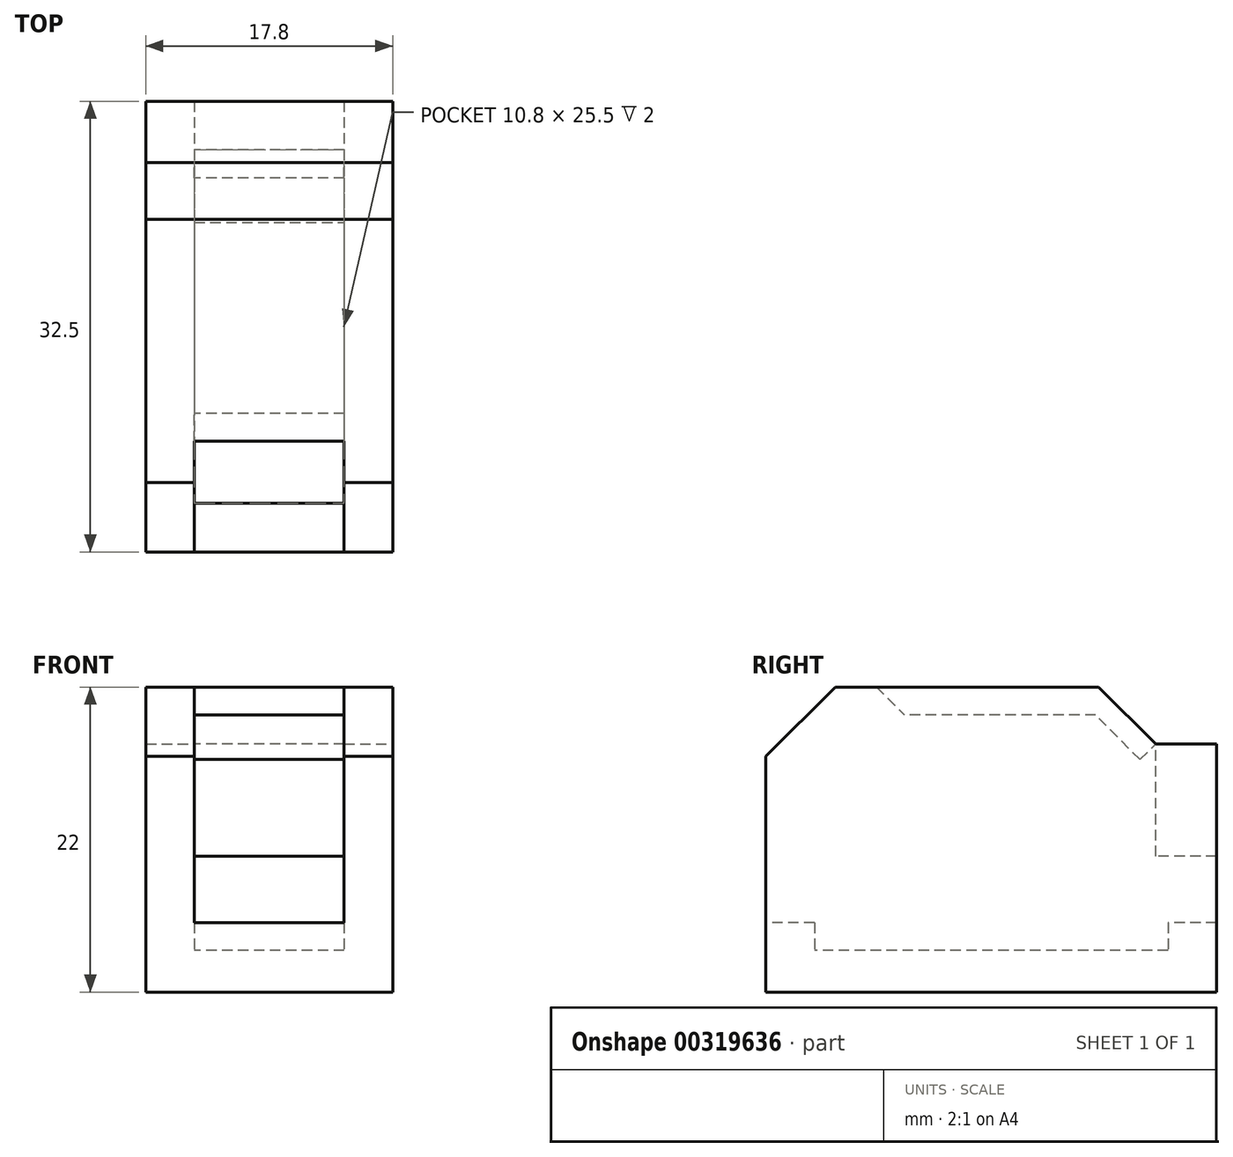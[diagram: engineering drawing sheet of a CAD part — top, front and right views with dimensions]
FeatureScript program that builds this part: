
annotation { "Feature Type Name" : "Feature", "Feature Type Description" : "" }
export const myFeature = defineFeature(function(context is Context, id is Id, definition is map)
    precondition{}
    {
        {
            var Q0;
            Q0=qCreatedBy(makeId("Top.planeOp"),FACE);
            var sketch = newSketch(context, id + "F0", { "sketchPlane" : qUnion([Q0])});
            skLineSegment(sketch, "E0.bottom", {"start": v(5.4, 12.75) * mm, "end": v(-5.4, 12.75) * mm});
            skLineSegment(sketch, "E0.top", {"start": v(5.4, -12.75) * mm, "end": v(-5.4, -12.75) * mm});
            skLineSegment(sketch, "E0.left", {"start": v(5.4, 12.75) * mm, "end": v(5.4, -12.75) * mm});
            skLineSegment(sketch, "E0.right", {"start": v(-5.4, 12.75) * mm, "end": v(-5.4, -12.75) * mm});
            skPoint(sketch, "E0.middle", {"position": v(0, 0) * mm});
            skLineSegment(sketch, "E1.0", {"start": v(-8.9, 16.25) * mm, "end": v(-8.9, -16.25) * mm});
            skLineSegment(sketch, "E1.1", {"start": v(8.9, 16.25) * mm, "end": v(-8.9, 16.25) * mm});
            skLineSegment(sketch, "E1.2", {"start": v(8.9, 16.25) * mm, "end": v(8.9, -16.25) * mm});
            skLineSegment(sketch, "E1.3", {"start": v(8.9, -16.25) * mm, "end": v(-8.9, -16.25) * mm});
            skLineSegment(sketch, "E2", {"start": v(-8.9, 0) * mm, "end": v(-5.4, 0) * mm});
            skLineSegment(sketch, "E3", {"start": v(5.4, 0) * mm, "end": v(8.9, 0) * mm});
            skLineSegment(sketch, "E4", {"start": v(-5.4, -12.75) * mm, "end": v(-5.4, -16.25) * mm});
            skLineSegment(sketch, "E5", {"start": v(5.4, -12.75) * mm, "end": v(5.4, -16.25) * mm});
            skLineSegment(sketch, "E6", {"start": v(-5.4, 12.75) * mm, "end": v(-5.4, 16.25) * mm});
            skLineSegment(sketch, "E7", {"start": v(5.4, 12.75) * mm, "end": v(5.4, 16.25) * mm});
            skLineSegment(sketch, "E8", {"start": v(5.4, 12.75) * mm, "end": v(8.9, 12.75) * mm});
            skLineSegment(sketch, "E9", {"start": v(-5.4, 12.75) * mm, "end": v(-8.9, 12.75) * mm});
            skSolve(sketch);
        }
        {
            var Q0;
            {var subQ3=sQuery(id+"F0.wireOp",EDGE,"E0.bottom");Q0=makeQuery(id+"F0.imprint","IMPRINT",FACE,{"disambiguationData":[TD([[makeQuery(id+"F0.imprint","IMPRINT",EDGE,{"derivedFrom":subQ3}),1.0]])]});}
            extrude(context, id + "F1", {"entities" : qUnion([Q0]), "depth" : 3 * mm});
        }
        {
            var Q0;
            {var subQ4=sQuery(id+"F0.wireOp",EDGE,"E2");Q0=makeQuery(id+"F0.imprint","IMPRINT",FACE,{"disambiguationData":[TD([[makeQuery(id+"F0.imprint","IMPRINT",EDGE,{"derivedFrom":subQ4}),1.0]])]});}
            var Q1;
            {var subQ3=sQuery(id+"F0.wireOp",EDGE,"E3");Q1=makeQuery(id+"F0.imprint","IMPRINT",FACE,{"disambiguationData":[TD([[makeQuery(id+"F0.imprint","IMPRINT",EDGE,{"derivedFrom":subQ3}),1.0]])]});}
            var Q2;
            {var subQ0=sQuery(id+"F0.wireOp",EDGE,"E2");Q2=makeQuery(id+"F0.imprint","IMPRINT",FACE,{"disambiguationData":[TD([[makeQuery(id+"F0.imprint","IMPRINT",EDGE,{"derivedFrom":subQ0}),-1.0]])]});}
            var Q3;
            {var subQ0=sQuery(id+"F0.wireOp",EDGE,"E3");Q3=makeQuery(id+"F0.imprint","IMPRINT",FACE,{"disambiguationData":[TD([[makeQuery(id+"F0.imprint","IMPRINT",EDGE,{"derivedFrom":subQ0}),-1.0]])]});}
            extrude(context, id + "F2", {"entities" : qUnion([Q0, Q1, Q2, Q3]), "operationType" : NewBodyOperationType.ADD, "depth" : 22 * mm});
        }
        {
            var Q0;
            Q0=makeQuery(id+"F0.imprint","IMPRINT",FACE,{"disambiguationData":[TD([[makeQuery(id+"F0.imprint","IMPRINT",EDGE,{"derivedFrom":sQuery(id+"F0.wireOp",EDGE,"E0.bottom")}),-1.0]])]});
            var Q1;
            {var subQ4=sQuery(id+"F0.wireOp",EDGE,"E6");Q1=makeQuery(id+"F0.imprint","IMPRINT",FACE,{"disambiguationData":[TD([[makeQuery(id+"F0.imprint","IMPRINT",EDGE,{"derivedFrom":subQ4}),1.0]])]});}
            var Q2;
            {var subQ3=sQuery(id+"F0.wireOp",EDGE,"E7");Q2=makeQuery(id+"F0.imprint","IMPRINT",FACE,{"disambiguationData":[TD([[makeQuery(id+"F0.imprint","IMPRINT",EDGE,{"derivedFrom":subQ3}),-1.0]])]});}
            extrude(context, id + "F3", {"entities" : qUnion([Q0, Q1, Q2]), "operationType" : NewBodyOperationType.ADD, "depth" : 5 * mm});
        }
        {
            var Q0;
            {var subQ0=sQuery(id+"F0.wireOp",EDGE,"E1.3");Q0=makeQuery(id+"F2.opExtrude","CAP_EDGE",EDGE,{"disambiguationData":[OSD([subQ0]),TDD([makeQuery(id+"F0.imprint","IMPRINT",EDGE,{"disambiguationData":[TD([[makeQuery(id+"F0.imprint","INTERSECT",VERTEX,{"derivedFrom":[sQuery(id+"F0.wireOp",EDGE,"E1.0"),subQ0]}),1.0]])],"derivedFrom":subQ0})])],"isStart":false});}
            var Q1;
            {var subQ0=sQuery(id+"F0.wireOp",EDGE,"E1.3");Q1=makeQuery(id+"F2.opExtrude","CAP_EDGE",EDGE,{"disambiguationData":[OSD([subQ0]),TDD([makeQuery(id+"F0.imprint","IMPRINT",EDGE,{"disambiguationData":[TD([[makeQuery(id+"F0.imprint","INTERSECT",VERTEX,{"derivedFrom":[sQuery(id+"F0.wireOp",EDGE,"E1.2"),subQ0]}),-1.0]])],"derivedFrom":subQ0})])],"isStart":false});}
            chamfer(context, id + "F4", {"entities" : qUnion([Q0, Q1]), "width" : 5 * mm, "tangentPropagation" : true});
        }
        {
            var Q0;
            {var subQ4=sQuery(id+"F0.wireOp",EDGE,"E6");Q0=makeQuery(id+"F0.imprint","IMPRINT",FACE,{"disambiguationData":[TD([[makeQuery(id+"F0.imprint","IMPRINT",EDGE,{"derivedFrom":subQ4}),1.0]])]});}
            var Q1;
            {var subQ3=sQuery(id+"F0.wireOp",EDGE,"E7");Q1=makeQuery(id+"F0.imprint","IMPRINT",FACE,{"disambiguationData":[TD([[makeQuery(id+"F0.imprint","IMPRINT",EDGE,{"derivedFrom":subQ3}),-1.0]])]});}
            extrude(context, id + "F5", {"entities" : qUnion([Q0, Q1]), "operationType" : NewBodyOperationType.ADD, "depth" : 17.9 * mm});
        }
        {
            var Q0;
            Q0=makeQuery(id+"F2.opExtrude","CAP_EDGE",EDGE,{"disambiguationData":[OSD([sQuery(id+"F0.wireOp",EDGE,"E8")])],"isStart":false});
            var Q1;
            Q1=makeQuery(id+"F2.opExtrude","CAP_EDGE",EDGE,{"disambiguationData":[OSD([sQuery(id+"F0.wireOp",EDGE,"E9")])],"isStart":false});
            chamfer(context, id + "F6", {"entities" : qUnion([Q0, Q1]), "width" : 5 * mm, "tangentPropagation" : true});
        }
        {
            var Q0;
            Q0=makeQuery(id+"F5.opExtrude","CAP_FACE",FACE,{"disambiguationData":[OSD([sQuery(id+"F0.wireOp",EDGE,"E1.1"),sQuery(id+"F0.wireOp",EDGE,"E1.2"),sQuery(id+"F0.wireOp",EDGE,"E7"),sQuery(id+"F0.wireOp",EDGE,"E8")])],"isStart":false});
            var sketch = newSketch(context, id + "F7", { "sketchPlane" : qUnion([Q0])});
            skLineSegment(sketch, "E10.bottom", {"start": v(8.9, 11.85) * mm, "end": v(-8.9, 11.85) * mm});
            skLineSegment(sketch, "E10.top", {"start": v(8.9, 16.25) * mm, "end": v(-8.9, 16.25) * mm});
            skLineSegment(sketch, "E10.left", {"start": v(8.9, 11.85) * mm, "end": v(8.9, 16.25) * mm});
            skLineSegment(sketch, "E10.right", {"start": v(-8.9, 11.85) * mm, "end": v(-8.9, 16.25) * mm});
            skSolve(sketch);
        }
        {
            var Q0;
            Q0=makeQuery(id+"F7.imprint","IMPRINT",FACE,{"disambiguationData":[TD([[makeQuery(id+"F7.imprint","IMPRINT",EDGE,{"derivedFrom":sQuery(id+"F7.wireOp",EDGE,"E10.top")}),1.0]])]});
            var Q1;
            {var subQ3=sQuery(id+"F7.wireOp",EDGE,"E10.left");Q1=makeQuery(id+"F7.imprint","IMPRINT",FACE,{"disambiguationData":[TD([[makeQuery(id+"F7.imprint","IMPRINT",EDGE,{"derivedFrom":subQ3}),-1.0]])]});}
            extrude(context, id + "F8", {"entities" : qUnion([Q0, Q1]), "operationType" : NewBodyOperationType.ADD, "oppositeDirection" : true, "depth" : 8.1 * mm});
        }
        {
            var Q0;
            Q0=makeQuery(id+"F6.opChamfer","BLEND_FACE",FACE,{"disambiguationData":[OSD([sQuery(id+"F0.wireOp",EDGE,"E8")])]});
            var sketch = newSketch(context, id + "F9", { "sketchPlane" : qUnion([Q0])});
            skLineSegment(sketch, "E11.bottom", {"start": v(-8.9, 10.08) * mm, "end": v(8.9, 10.08) * mm});
            skLineSegment(sketch, "E11.top", {"start": v(-8.9, 4.28) * mm, "end": v(8.9, 4.28) * mm});
            skLineSegment(sketch, "E11.left", {"start": v(-8.9, 10.08) * mm, "end": v(-8.9, 4.28) * mm});
            skLineSegment(sketch, "E11.right", {"start": v(8.9, 10.08) * mm, "end": v(8.9, 4.28) * mm});
            skSolve(sketch);
        }
        {
            var Q0;
            {var subQ4=sQuery(id+"F9.wireOp",EDGE,"E11.left");Q0=makeQuery(id+"F9.imprint","IMPRINT",FACE,{"disambiguationData":[TD([[makeQuery(id+"F9.imprint","IMPRINT",EDGE,{"derivedFrom":subQ4}),-1.0]])]});}
            var Q1;
            {var subQ3=sQuery(id+"F9.wireOp",EDGE,"E11.right");Q1=makeQuery(id+"F9.imprint","IMPRINT",FACE,{"disambiguationData":[TD([[makeQuery(id+"F9.imprint","IMPRINT",EDGE,{"derivedFrom":subQ3}),-1.0]])]});}
            extrude(context, id + "F10", {"entities" : qUnion([Q0, Q1]), "operationType" : NewBodyOperationType.ADD, "oppositeDirection" : true, "depth" : 1.59 * mm});
        }
        {
            var Q0;
            Q0=makeQuery(id+"F0.imprint","IMPRINT",FACE,{"disambiguationData":[TD([[makeQuery(id+"F0.imprint","IMPRINT",EDGE,{"derivedFrom":sQuery(id+"F0.wireOp",EDGE,"E0.top")}),1.0]])]});
            extrude(context, id + "F11", {"entities" : qUnion([Q0]), "operationType" : NewBodyOperationType.ADD, "depth" : 5 * mm});
        }
        {
            var Q0;
            Q0=makeQuery(id+"F2.opExtrude","CAP_FACE",FACE,{"disambiguationData":[OSD([sQuery(id+"F0.wireOp",EDGE,"E0.left"),sQuery(id+"F0.wireOp",EDGE,"E1.2"),sQuery(id+"F0.wireOp",EDGE,"E1.3"),sQuery(id+"F0.wireOp",EDGE,"E5"),sQuery(id+"F0.wireOp",EDGE,"E8")])],"isStart":false});
            var sketch = newSketch(context, id + "F12", { "sketchPlane" : qUnion([Q0])});
            skLineSegment(sketch, "E12.bottom", {"start": v(8.9, 7.75) * mm, "end": v(-8.9, 7.75) * mm});
            skLineSegment(sketch, "E12.top", {"start": v(8.9, -11.25) * mm, "end": v(-8.9, -11.25) * mm});
            skLineSegment(sketch, "E12.left", {"start": v(8.9, 7.75) * mm, "end": v(8.9, -11.25) * mm});
            skLineSegment(sketch, "E12.right", {"start": v(-8.9, 7.75) * mm, "end": v(-8.9, -11.25) * mm});
            skSolve(sketch);
        }
        {
            var Q0;
            {var subQ2=sQuery(id+"F12.wireOp",EDGE,"E12.right");Q0=makeQuery(id+"F12.imprint","IMPRINT",FACE,{"disambiguationData":[TD([[makeQuery(id+"F12.imprint","IMPRINT",EDGE,{"derivedFrom":subQ2}),1.0]])]});}
            extrude(context, id + "F13", {"entities" : qUnion([Q0]), "operationType" : NewBodyOperationType.ADD, "oppositeDirection" : true, "depth" : 2.02 * mm});
        }
        {
            var Q0;
            Q0=makeQuery(id+"F13.opExtrude","CAP_EDGE",EDGE,{"disambiguationData":[OSD([sQuery(id+"F12.wireOp",EDGE,"E12.top")])],"isStart":false});
            chamfer(context, id + "F14", {"entities" : qUnion([Q0]), "width" : 5 * mm, "tangentPropagation" : true});
        }
    });
